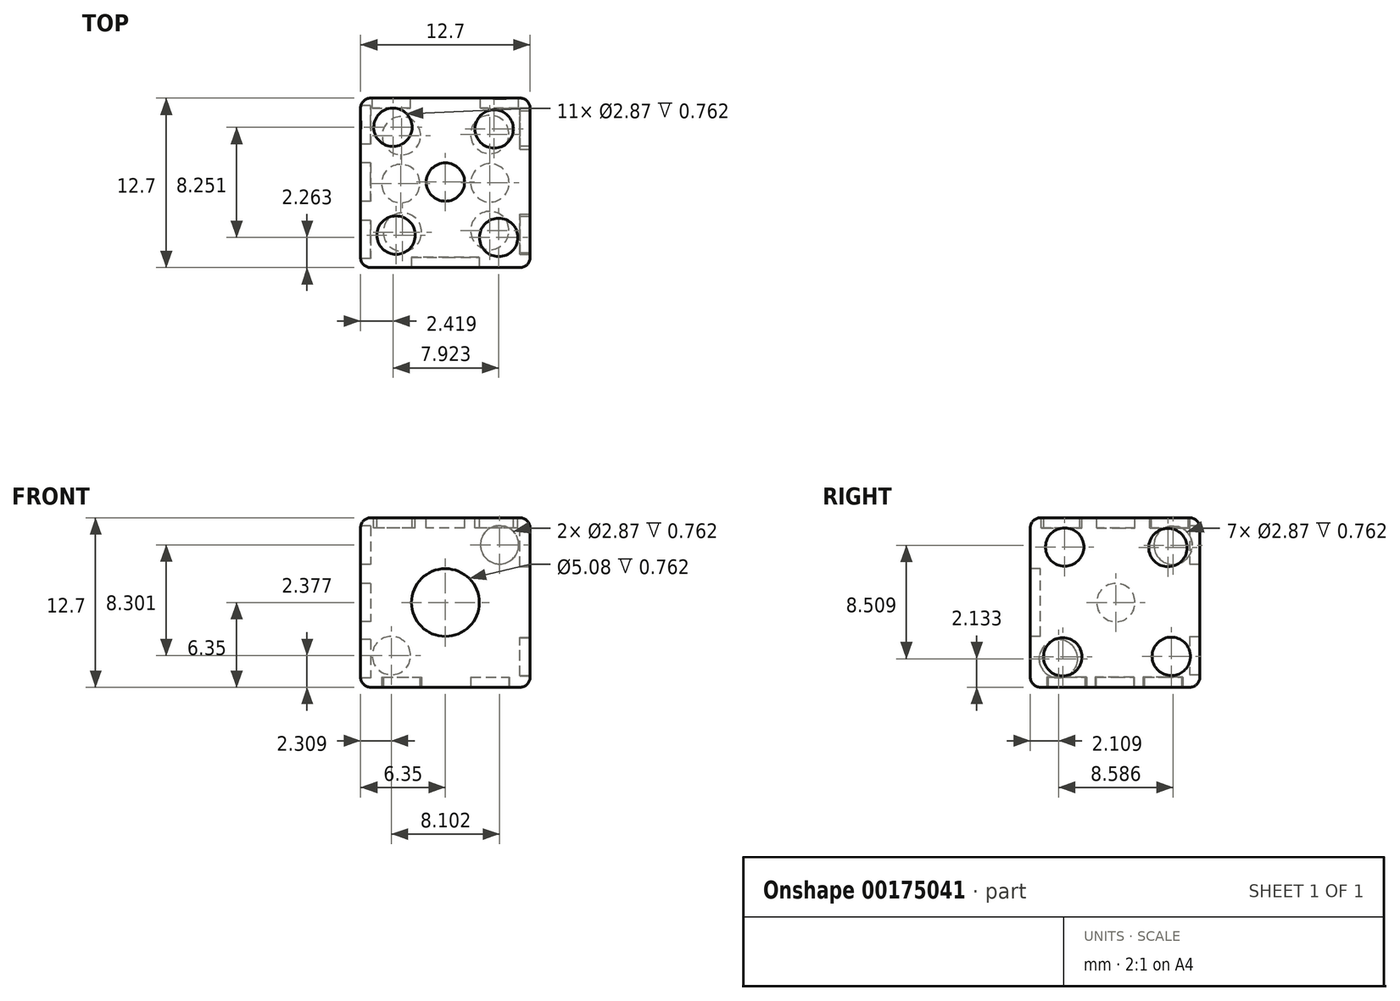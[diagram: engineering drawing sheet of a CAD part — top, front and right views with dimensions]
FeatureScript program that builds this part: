
annotation { "Feature Type Name" : "Feature", "Feature Type Description" : "" }
export const myFeature = defineFeature(function(context is Context, id is Id, definition is map)
    precondition{}
    {
        {
            var Q0;
            Q0=qCreatedBy(makeId("Front.planeOp"),FACE);
            var sketch = newSketch(context, id + "F0", { "sketchPlane" : qUnion([Q0])});
            skLineSegment(sketch, "E0.bottom", {"start": v(-6.35, 6.35) * mm, "end": v(6.35, 6.35) * mm});
            skLineSegment(sketch, "E0.top", {"start": v(-6.35, -6.35) * mm, "end": v(6.35, -6.35) * mm});
            skLineSegment(sketch, "E0.left", {"start": v(-6.35, 6.35) * mm, "end": v(-6.35, -6.35) * mm});
            skLineSegment(sketch, "E0.right", {"start": v(6.35, 6.35) * mm, "end": v(6.35, -6.35) * mm});
            skSolve(sketch);
        }
        {
            var Q0;
            Q0 = qSketchRegion(id + "F0", true);
            extrude(context, id + "F1", {"entities" : qUnion([Q0]), "depth" : 12.7 * mm});
        }
        {
            var Q0;
            Q0=makeQuery(id+"F1.opExtrude","CAP_FACE",FACE,{"disambiguationData":[OSD([sQuery(id+"F0.wireOp",EDGE,"E0.bottom"),sQuery(id+"F0.wireOp",EDGE,"E0.top"),sQuery(id+"F0.wireOp",EDGE,"E0.left"),sQuery(id+"F0.wireOp",EDGE,"E0.right")])],"isStart":false});
            var sketch = newSketch(context, id + "F2", { "sketchPlane" : qUnion([Q0])});
            skCircle(sketch, "E1", {"center": v(0, 0) * mm, "radius": 2.54 * mm});
            skSolve(sketch);
        }
        {
            var Q0;
            Q0 = qSketchRegion(id + "F2", true);
            extrude(context, id + "F3", {"entities" : qUnion([Q0]), "operationType" : NewBodyOperationType.REMOVE, "oppositeDirection" : true, "depth" : 0.76 * mm});
        }
        {
            var Q0;
            Q0=makeQuery(id+"F1.opExtrude","CAP_FACE",FACE,{"disambiguationData":[OSD([sQuery(id+"F0.wireOp",EDGE,"E0.bottom"),sQuery(id+"F0.wireOp",EDGE,"E0.top"),sQuery(id+"F0.wireOp",EDGE,"E0.left"),sQuery(id+"F0.wireOp",EDGE,"E0.right")])],"isStart":true});
            var sketch = newSketch(context, id + "F4", { "sketchPlane" : qUnion([Q0])});
            skCircle(sketch, "E2", {"center": v(-4.06, 4.33) * mm, "radius": 1.44 * mm});
            skCircle(sketch, "E3", {"center": v(4.04, -3.97) * mm, "radius": 1.44 * mm});
            skSolve(sketch);
        }
        {
            var Q0;
            Q0 = qSketchRegion(id + "F4", true);
            extrude(context, id + "F5", {"entities" : qUnion([Q0]), "operationType" : NewBodyOperationType.REMOVE, "oppositeDirection" : true, "depth" : 0.76 * mm});
        }
        {
            var Q0;
            Q0=makeQuery(id+"F1.opExtrude","SWEPT_FACE",FACE,{"disambiguationData":[OSD([sQuery(id+"F0.wireOp",EDGE,"E0.left")])]});
            var sketch = newSketch(context, id + "F6", { "sketchPlane" : qUnion([Q0])});
            skCircle(sketch, "E4", {"center": v(6.29, 0) * mm, "radius": 1.44 * mm});
            skCircle(sketch, "E5", {"center": v(10.6, -4.22) * mm, "radius": 1.44 * mm});
            skCircle(sketch, "E6", {"center": v(2, 4.3) * mm, "radius": 1.44 * mm});
            skSolve(sketch);
        }
        {
            var Q0;
            Q0 = qSketchRegion(id + "F6", true);
            extrude(context, id + "F7", {"entities" : qUnion([Q0]), "operationType" : NewBodyOperationType.REMOVE, "oppositeDirection" : true, "depth" : 0.76 * mm});
        }
        {
            var Q0;
            Q0=makeQuery(id+"F1.opExtrude","SWEPT_FACE",FACE,{"disambiguationData":[OSD([sQuery(id+"F0.wireOp",EDGE,"E0.right")])]});
            var sketch = newSketch(context, id + "F8", { "sketchPlane" : qUnion([Q0])});
            skCircle(sketch, "E7", {"center": v(-10.12, 4.16) * mm, "radius": 1.44 * mm});
            skCircle(sketch, "E8", {"center": v(-2.4, 4.12) * mm, "radius": 1.44 * mm});
            skCircle(sketch, "E9", {"center": v(-10.27, -4.07) * mm, "radius": 1.44 * mm});
            skCircle(sketch, "E10", {"center": v(-2.14, -4.03) * mm, "radius": 1.44 * mm});
            skSolve(sketch);
        }
        {
            var Q0;
            Q0 = qSketchRegion(id + "F8", true);
            extrude(context, id + "F9", {"entities" : qUnion([Q0]), "operationType" : NewBodyOperationType.REMOVE, "oppositeDirection" : true, "depth" : 0.76 * mm});
        }
        {
            var Q0;
            Q0=makeQuery(id+"F1.opExtrude","SWEPT_FACE",FACE,{"disambiguationData":[OSD([sQuery(id+"F0.wireOp",EDGE,"E0.bottom")])]});
            var sketch = newSketch(context, id + "F10", { "sketchPlane" : qUnion([Q0])});
            skCircle(sketch, "E11", {"center": v(0, -6.29) * mm, "radius": 1.44 * mm});
            skCircle(sketch, "E12", {"center": v(3.65, -2.31) * mm, "radius": 1.44 * mm});
            skCircle(sketch, "E13", {"center": v(-3.93, -2.19) * mm, "radius": 1.44 * mm});
            skCircle(sketch, "E14", {"center": v(-3.7, -10.26) * mm, "radius": 1.44 * mm});
            skCircle(sketch, "E15", {"center": v(4, -10.44) * mm, "radius": 1.44 * mm});
            skSolve(sketch);
        }
        {
            var Q0;
            Q0 = qSketchRegion(id + "F10", true);
            extrude(context, id + "F11", {"entities" : qUnion([Q0]), "operationType" : NewBodyOperationType.REMOVE, "oppositeDirection" : true, "depth" : 0.76 * mm});
        }
        {
            var Q0;
            Q0=makeQuery(id+"F1.opExtrude","CAP_EDGE",EDGE,{"disambiguationData":[OSD([sQuery(id+"F0.wireOp",EDGE,"E0.bottom")])],"isStart":false});
            var Q1;
            Q1=makeQuery(id+"F1.opExtrude","SWEPT_EDGE",EDGE,{"disambiguationData":[OSD([sQuery(id+"F0.wireOp",EDGE,"E0.bottom"),sQuery(id+"F0.wireOp",EDGE,"E0.left")])]});
            var Q2;
            Q2=makeQuery(id+"F1.opExtrude","CAP_EDGE",EDGE,{"disambiguationData":[OSD([sQuery(id+"F0.wireOp",EDGE,"E0.bottom")])],"isStart":true});
            var Q3;
            Q3=makeQuery(id+"F1.opExtrude","SWEPT_EDGE",EDGE,{"disambiguationData":[OSD([sQuery(id+"F0.wireOp",EDGE,"E0.bottom"),sQuery(id+"F0.wireOp",EDGE,"E0.right")])]});
            var Q4;
            Q4=makeQuery(id+"F1.opExtrude","CAP_EDGE",EDGE,{"disambiguationData":[OSD([sQuery(id+"F0.wireOp",EDGE,"E0.right")])],"isStart":false});
            var Q5;
            Q5=makeQuery(id+"F1.opExtrude","CAP_EDGE",EDGE,{"disambiguationData":[OSD([sQuery(id+"F0.wireOp",EDGE,"E0.left")])],"isStart":false});
            var Q6;
            Q6=makeQuery(id+"F1.opExtrude","CAP_EDGE",EDGE,{"disambiguationData":[OSD([sQuery(id+"F0.wireOp",EDGE,"E0.top")])],"isStart":false});
            var Q7;
            Q7=makeQuery(id+"F1.opExtrude","SWEPT_EDGE",EDGE,{"disambiguationData":[OSD([sQuery(id+"F0.wireOp",EDGE,"E0.top"),sQuery(id+"F0.wireOp",EDGE,"E0.right")])]});
            var Q8;
            Q8=makeQuery(id+"F1.opExtrude","CAP_EDGE",EDGE,{"disambiguationData":[OSD([sQuery(id+"F0.wireOp",EDGE,"E0.right")])],"isStart":true});
            var Q9;
            Q9=makeQuery(id+"F1.opExtrude","CAP_EDGE",EDGE,{"disambiguationData":[OSD([sQuery(id+"F0.wireOp",EDGE,"E0.left")])],"isStart":true});
            var Q10;
            Q10=makeQuery(id+"F1.opExtrude","CAP_EDGE",EDGE,{"disambiguationData":[OSD([sQuery(id+"F0.wireOp",EDGE,"E0.top")])],"isStart":true});
            var Q11;
            Q11=makeQuery(id+"F1.opExtrude","SWEPT_EDGE",EDGE,{"disambiguationData":[OSD([sQuery(id+"F0.wireOp",EDGE,"E0.top"),sQuery(id+"F0.wireOp",EDGE,"E0.left")])]});
            fillet(context, id + "F12", {"entities" : qUnion([Q0, Q1, Q2, Q3, Q4, Q5, Q6, Q7, Q8, Q9, Q10, Q11]), "radius" : 0.76 * mm, "tangentPropagation" : true, "allowEdgeOverflow" : false});
        }
        {
            var Q0;
            Q0=makeQuery(id+"F1.opExtrude","SWEPT_FACE",FACE,{"disambiguationData":[OSD([sQuery(id+"F0.wireOp",EDGE,"E0.top")])]});
            var sketch = newSketch(context, id + "F13", { "sketchPlane" : qUnion([Q0])});
            skCircle(sketch, "E16", {"center": v(3.33, 6.35) * mm, "radius": 1.44 * mm});
            skPoint(sketch, "E16.centerSnap0", {"position": v(5.59, 6.35) * mm});
            skCircle(sketch, "E17", {"center": v(3.32, 9.92) * mm, "radius": 1.44 * mm});
            skCircle(sketch, "E18", {"center": v(3.32, 2.72) * mm, "radius": 1.44 * mm});
            skCircle(sketch, "E19", {"center": v(-3.22, 10.04) * mm, "radius": 1.44 * mm});
            skCircle(sketch, "E20", {"center": v(-3.35, 6.4) * mm, "radius": 1.44 * mm});
            skCircle(sketch, "E21", {"center": v(-3.3, 2.82) * mm, "radius": 1.44 * mm});
            skSolve(sketch);
        }
        {
            var Q0;
            Q0 = qSketchRegion(id + "F13", true);
            extrude(context, id + "F14", {"entities" : qUnion([Q0]), "operationType" : NewBodyOperationType.REMOVE, "oppositeDirection" : true, "depth" : 0.76 * mm});
        }
    });
